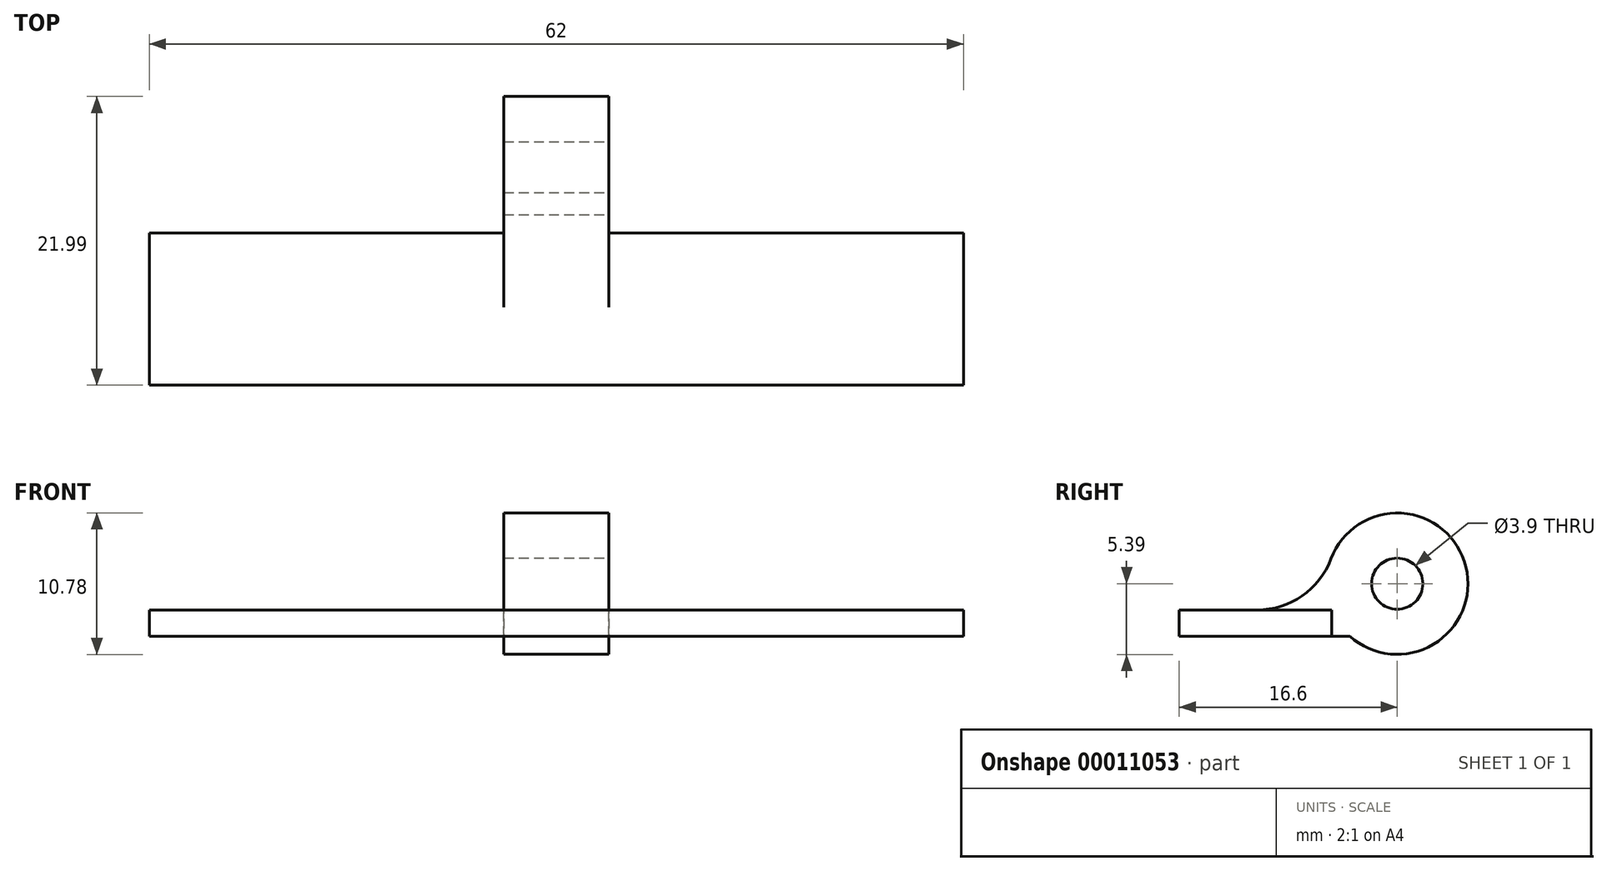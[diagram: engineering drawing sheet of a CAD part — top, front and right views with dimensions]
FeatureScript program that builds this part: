
annotation { "Feature Type Name" : "Feature", "Feature Type Description" : "" }
export const myFeature = defineFeature(function(context is Context, id is Id, definition is map)
    precondition{}
    {
        {
            var Q0;
            Q0=qCreatedBy(makeId("Top.planeOp"),FACE);
            var sketch = newSketch(context, id + "F0", { "sketchPlane" : qUnion([Q0])});
            skLineSegment(sketch, "E0.top", {"start": v(0, 11.6) * mm, "end": v(62, 11.6) * mm});
            skLineSegment(sketch, "E0.left", {"start": v(0, 0) * mm, "end": v(0, 11.6) * mm});
            skLineSegment(sketch, "E0.right", {"start": v(62, 0) * mm, "end": v(62, 11.6) * mm});
            skLineSegment(sketch, "E1", {"start": v(0, 0) * mm, "end": v(62, 0) * mm});
            skSolve(sketch);
        }
        {
            var Q0;
            Q0=makeQuery(id+"F0.imprint","IMPRINT",FACE,{"disambiguationData":[TD([[makeQuery(id+"F0.imprint","IMPRINT",EDGE,{"derivedFrom":sQuery(id+"F0.wireOp",EDGE,"E0.bottom")}),1.0]])]});
            var Q1;
            Q1=makeQuery(id+"F0.imprint","IMPRINT",FACE,{"disambiguationData":[TD([[makeQuery(id+"F0.imprint","IMPRINT",EDGE,{"derivedFrom":sQuery(id+"F0.wireOp",EDGE,"E0.top")}),-1.0]])]});
            extrude(context, id + "F1", {"entities" : qUnion([Q0, Q1]), "depth" : 2 * mm});
        }
        {
            var Q0;
            Q0=makeQuery(id+"F1.opExtrude","SWEPT_FACE",FACE,{"disambiguationData":[OSD([sQuery(id+"F0.wireOp",EDGE,"E0.left")])]});
            var Q1;
            Q1=makeQuery(id+"F1.opExtrude","SWEPT_FACE",FACE,{"disambiguationData":[OSD([sQuery(id+"F0.wireOp",EDGE,"E0.right")])]});
            cPlane(context, id + "F2", {"entities" : qUnion([Q0, Q1]), "cplaneType" : CPlaneType.MID_PLANE, "offset" : 150 * mm, "width" : 150 * mm, "height" : 150 * mm});
        }
        {
            var Q0;
            Q0=qCreatedBy(id+"F2.planeOp",FACE);
            var sketch = newSketch(context, id + "F3", { "sketchPlane" : qUnion([Q0])});
            skCircle(sketch, "E2", {"center": v(-16.6, 4) * mm, "radius": 1.95 * mm});
            skPoint(sketch, "E3.0", {"position": v(-11.6, 2) * mm});
            skArc(sketch, "E4", {"start": v(-11.6, 2) * mm, "mid": v(-21.02, 7.08) * mm, "end": v(-13, 0) * mm});
            skLineSegment(sketch, "E5", {"start": v(-11.6, 0) * mm, "end": v(-13, 0) * mm});
            skLineSegment(sketch, "E6", {"start": v(-11.6, 0) * mm, "end": v(-11.6, 2) * mm});
            skSolve(sketch);
        }
        {
            var Q0;
            Q0=makeQuery(id+"F3.imprint","IMPRINT",FACE,{"disambiguationData":[TD([[makeQuery(id+"F3.imprint","IMPRINT",EDGE,{"derivedFrom":sQuery(id+"F3.wireOp",EDGE,"E2")}),-1.0]])]});
            extrude(context, id + "F4", {"entities" : qUnion([Q0]), "operationType" : NewBodyOperationType.ADD, "depth" : 4 * mm, "hasSecondDirection" : true, "secondDirectionOppositeDirection" : true, "secondDirectionDepth" : 4 * mm});
        }
        {
            var Q0;
            Q0=makeQuery(id+"F4.boolean.opBoolean","MERGE",EDGE,{"derivedFrom":[makeQuery(id+"F1.opExtrude","CAP_EDGE",EDGE,{"disambiguationData":[OSD([sQuery(id+"F0.wireOp",EDGE,"E0.top")])],"isStart":false}),makeQuery(id+"F4.opExtrude","SWEPT_EDGE",EDGE,{"disambiguationData":[OSD([sQuery(id+"F3.wireOp",EDGE,"E4"),sQuery(id+"F3.wireOp",EDGE,"E6")])]})]});
            fillet(context, id + "F5", {"entities" : qUnion([Q0]), "radius" : 6 * mm, "tangentPropagation" : true, "allowEdgeOverflow" : false});
        }
    });
